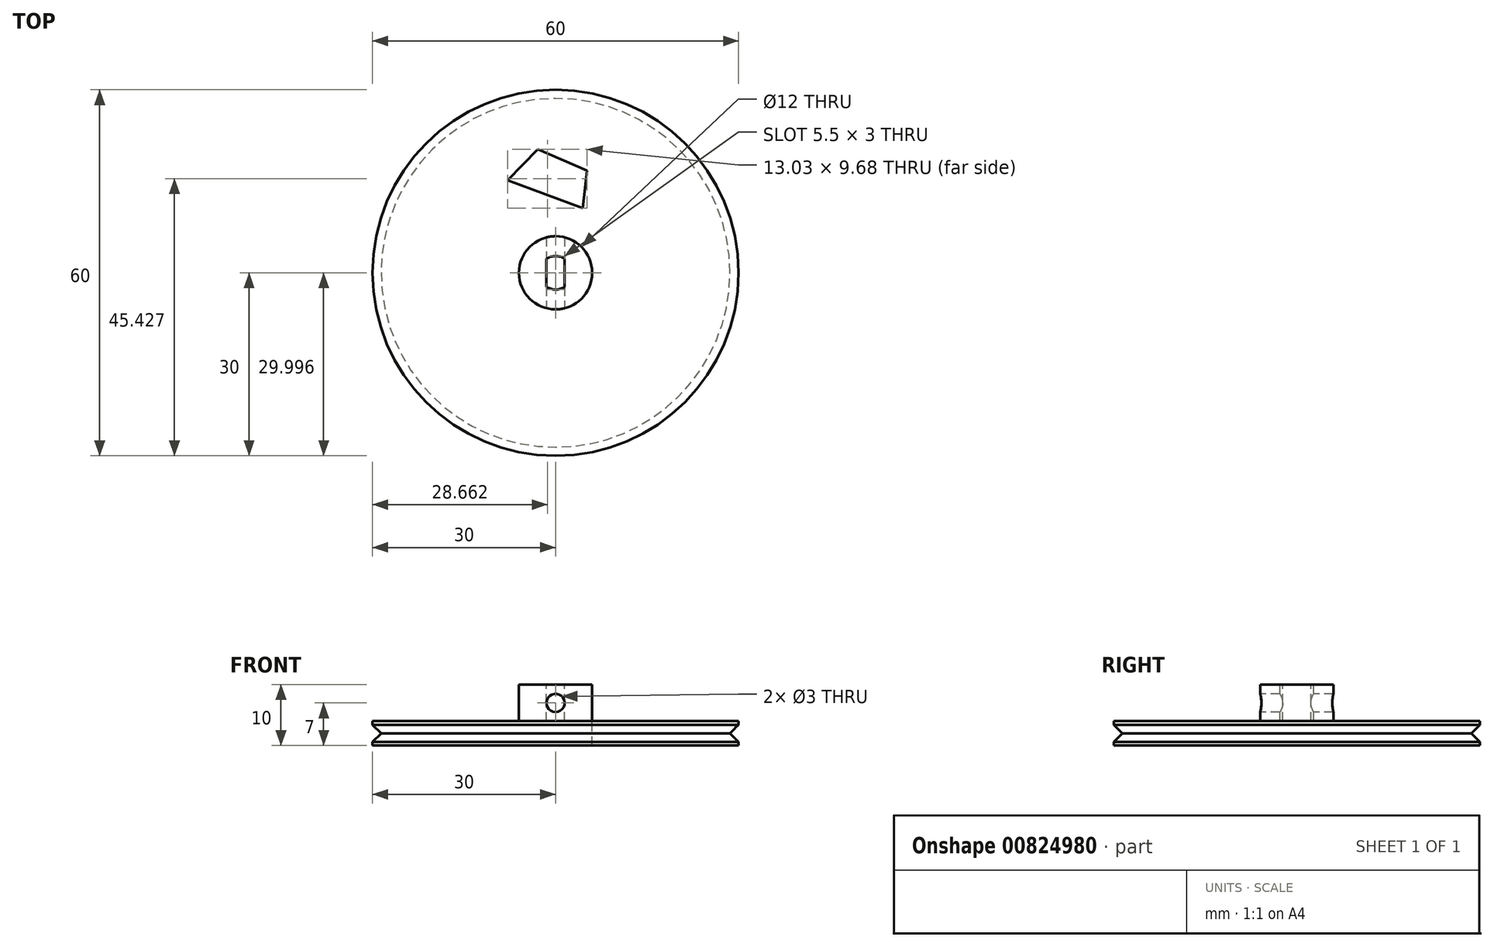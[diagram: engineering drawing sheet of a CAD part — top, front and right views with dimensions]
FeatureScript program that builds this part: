
annotation { "Feature Type Name" : "Feature", "Feature Type Description" : "" }
export const myFeature = defineFeature(function(context is Context, id is Id, definition is map)
    precondition{}
    {
        {
            var Q0;
            Q0=qCreatedBy(makeId("Top.planeOp"),FACE);
            var sketch = newSketch(context, id + "F0", { "sketchPlane" : qUnion([Q0])});
            skCircle(sketch, "E0", {"center": v(0, 0) * mm, "radius": 30 * mm});
            skCircle(sketch, "E1", {"center": v(0, 0) * mm, "radius": 6 * mm});
            skSolve(sketch);
        }
        {
            var Q0;
            Q0=makeQuery(id+"F0.imprint","IMPRINT",FACE,{"disambiguationData":[TD([[makeQuery(id+"F0.imprint","IMPRINT",EDGE,{"derivedFrom":sQuery(id+"F0.wireOp",EDGE,"E0")}),1.0]])]});
            extrude(context, id + "F1", {"entities" : qUnion([Q0]), "oppositeDirection" : true, "depth" : 4 * mm, "offsetDistance" : 25 * mm});
        }
        {
            var Q0;
            Q0=makeQuery(id+"F0.imprint","IMPRINT",FACE,{"disambiguationData":[TD([[makeQuery(id+"F0.imprint","IMPRINT",EDGE,{"derivedFrom":sQuery(id+"F0.wireOp",EDGE,"E1")}),1.0]])]});
            extrude(context, id + "F2", {"entities" : qUnion([Q0]), "depth" : 6 * mm, "offsetDistance" : 25 * mm});
        }
        {
            var Q0;
            Q0=qCreatedBy(makeId("Front.planeOp"),FACE);
            var sketch = newSketch(context, id + "F3", { "sketchPlane" : qUnion([Q0])});
            skCircle(sketch, "E2", {"center": v(0, 3) * mm, "radius": 1.5 * mm});
            skSolve(sketch);
        }
        {
            var Q0;
            Q0=qSketchRegion(id+"F3",true);
            extrude(context, id + "F4", {"entities" : qUnion([Q0]), "operationType" : NewBodyOperationType.REMOVE, "endBound" : BoundingType.SYMMETRIC, "oppositeDirection" : true, "depth" : 25 * mm, "offsetDistance" : 25 * mm});
        }
        {
            var Q0;
            Q0=makeQuery(id+"F2.opExtrude","CAP_FACE",FACE,{"disambiguationData":[OSD([sQuery(id+"F0.wireOp",EDGE,"E1")])],"isStart":false});
            var sketch = newSketch(context, id + "F5", { "sketchPlane" : qUnion([Q0])});
            skLineSegment(sketch, "E3.bottom", {"start": v(-1.5, -2.3) * mm, "end": v(1.5, -2.3) * mm});
            skLineSegment(sketch, "E3.top", {"start": v(-1.5, 2.3) * mm, "end": v(1.5, 2.3) * mm});
            skLineSegment(sketch, "E3.left", {"start": v(-1.5, -2.3) * mm, "end": v(-1.5, 2.3) * mm});
            skLineSegment(sketch, "E3.right", {"start": v(1.5, -2.3) * mm, "end": v(1.5, 2.3) * mm});
            skPoint(sketch, "E3.middle", {"position": v(0, 0) * mm});
            skArc(sketch, "E4", {"start": v(1.5, 2.3) * mm, "mid": v(0, 2.75) * mm, "end": v(-1.5, 2.3) * mm});
            skArc(sketch, "E5", {"start": v(-1.5, -2.3) * mm, "mid": v(0, -2.75) * mm, "end": v(1.5, -2.3) * mm});
            skSolve(sketch);
        }
        {
            var Q0;
            Q0=qSketchRegion(id+"F5",true);
            extrude(context, id + "F6", {"entities" : qUnion([Q0]), "operationType" : NewBodyOperationType.REMOVE, "oppositeDirection" : true, "depth" : 9.4 * mm, "offsetDistance" : 25 * mm});
        }
        {
            var Q0;
            Q0=qCreatedBy(makeId("Front.planeOp"),FACE);
            var sketch = newSketch(context, id + "F7", { "sketchPlane" : qUnion([Q0])});
            skLineSegment(sketch, "E6.0", {"start": v(-30, 0) * mm, "end": v(30, 0) * mm});
            skLineSegment(sketch, "E7", {"start": v(30, 0) * mm, "end": v(30, -4) * mm});
            skLineSegment(sketch, "E8", {"start": v(-30, -4) * mm, "end": v(-30, 0) * mm});
            skLineSegment(sketch, "E9", {"start": v(-30, -0.59) * mm, "end": v(-28.59, -2) * mm});
            skLineSegment(sketch, "E10", {"start": v(-28.59, -2) * mm, "end": v(-30, -3.41) * mm});
            skLineSegment(sketch, "E11", {"start": v(-30, -2) * mm, "end": v(-21.36, -2) * mm, "construction": true});
            skPoint(sketch, "E11.endSnap0", {"position": v(-30, -2) * mm});
            skLineSegment(sketch, "E12", {"start": v(0, 10.47) * mm, "end": v(0, -7.56) * mm, "construction": true});
            skSolve(sketch);
        }
        {
            var Q0;
            Q0=qSketchRegion(id+"F7",true);
            var Q1;
            Q1=sQuery(id+"F7.wireOp",EDGE,"E9");
            var Q2;
            Q2=sQuery(id+"F7.wireOp",EDGE,"E10");
            var Q3;
            Q3=sQuery(id+"F7.wireOp",EDGE,"E12");
            revolve(context, id + "F8", {"operationType" : NewBodyOperationType.REMOVE, "surfaceOperationType" : NewSurfaceOperationType.NEW, "entities" : qUnion([Q0]), "surfaceEntities" : qUnion([Q1, Q2]), "axis" : qUnion([Q3]), "revolveType" : RevolveType.FULL});
        }
        {
            var Q0;
            Q0=makeQuery(id+"F0.imprint","IMPRINT",FACE,{"disambiguationData":[TD([[makeQuery(id+"F0.imprint","IMPRINT",EDGE,{"derivedFrom":sQuery(id+"F0.wireOp",EDGE,"E0")}),1.0]])]});
            var sketch = newSketch(context, id + "F9", { "sketchPlane" : qUnion([Q0])});
            skLineSegment(sketch, "E13", {"start": v(0, 36.11) * mm, "end": v(0, 0) * mm, "construction": true});
            skCircle(sketch, "E14", {"center": v(0, 0) * mm, "radius": 28 * mm, "construction": true});
            skCircle(sketch, "E15", {"center": v(0, 0) * mm, "radius": 8 * mm, "construction": true});
            skLineSegment(sketch, "E16", {"start": v(-7.85, 15.16) * mm, "end": v(4.47, 10.59) * mm});
            skLineSegment(sketch, "E17", {"start": v(-7.85, 15.16) * mm, "end": v(-2.92, 20.27) * mm});
            skLineSegment(sketch, "E18", {"start": v(-2.92, 20.27) * mm, "end": v(5.18, 16.75) * mm});
            skLineSegment(sketch, "E19", {"start": v(4.47, 10.59) * mm, "end": v(5.18, 16.75) * mm});
            skSolve(sketch);
        }
        {
            var Q0;
            Q0=makeQuery(id+"F9.imprint","IMPRINT",FACE,{"disambiguationData":[TD([[makeQuery(id+"F9.imprint","IMPRINT",EDGE,{"derivedFrom":sQuery(id+"F9.wireOp",EDGE,"E16")}),1.0]])]});
            var Q1;
            Q1=makeQuery(id+"F1.opExtrude","CAP_FACE",FACE,{"disambiguationData":[OSD([sQuery(id+"F0.wireOp",EDGE,"E0"),sQuery(id+"F0.wireOp",EDGE,"E1")])],"isStart":false});
            extrude(context, id + "F10", {"entities" : qUnion([Q0]), "operationType" : NewBodyOperationType.REMOVE, "endBound" : BoundingType.UP_TO_SURFACE, "oppositeDirection" : true, "depth" : 25 * mm, "endBoundEntityFace" : qUnion([Q1]), "offsetDistance" : 25 * mm});
        }
    });
